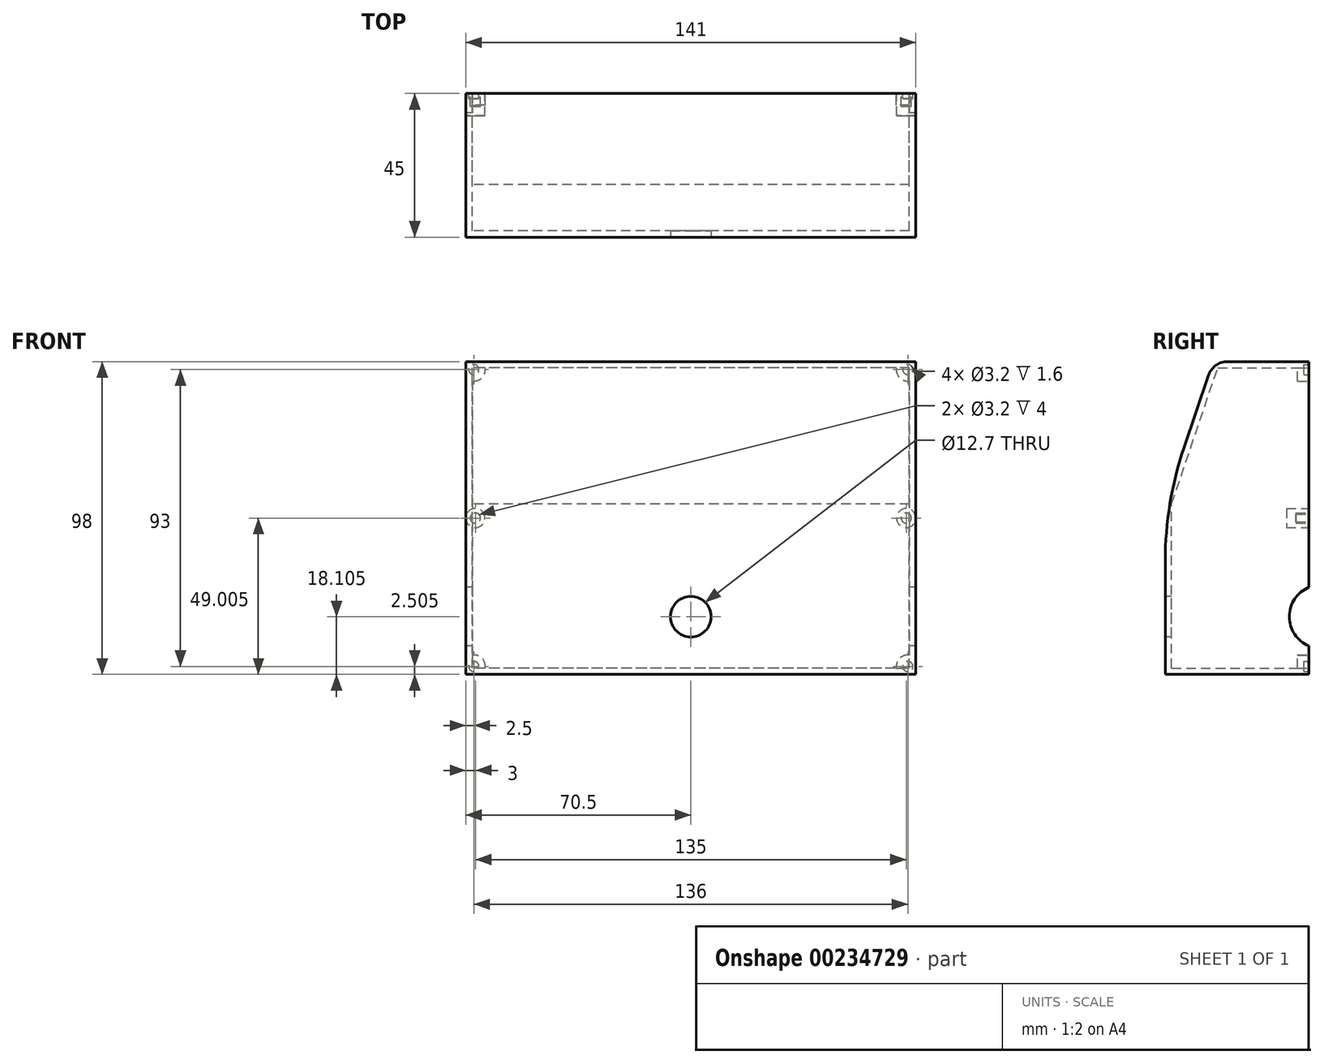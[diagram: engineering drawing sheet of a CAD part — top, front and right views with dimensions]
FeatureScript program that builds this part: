
annotation { "Feature Type Name" : "Feature", "Feature Type Description" : "" }
export const myFeature = defineFeature(function(context is Context, id is Id, definition is map)
    precondition{}
    {
        {
            var Q0;
            Q0=qCreatedBy(makeId("Right.planeOp"),FACE);
            var sketch = newSketch(context, id + "F0", { "sketchPlane" : qUnion([Q0])});
            skLineSegment(sketch, "E0.bottom", {"start": v(-27, 122.67) * mm, "end": v(33, 122.67) * mm});
            skLineSegment(sketch, "E0.top", {"start": v(-27, 24.67) * mm, "end": v(33, 24.67) * mm});
            skLineSegment(sketch, "E0.left", {"start": v(-27, 122.67) * mm, "end": v(-27, 24.67) * mm});
            skLineSegment(sketch, "E0.right", {"start": v(33, 122.67) * mm, "end": v(33, 24.67) * mm});
            skPoint(sketch, "E1", {"position": v(-12, 24.67) * mm});
            skPoint(sketch, "E2", {"position": v(-12, 78.42) * mm});
            skLineSegment(sketch, "E3", {"start": v(-12, 24.67) * mm, "end": v(-12, 78.42) * mm});
            skPoint(sketch, "E4", {"position": v(3, 122.67) * mm});
            skLineSegment(sketch, "E5", {"start": v(-12, 78.42) * mm, "end": v(3, 122.67) * mm});
            skSolve(sketch);
        }
        {
            var Q0;
            {var subQ0=sQuery(id+"F0.wireOp",EDGE,"E0.right");Q0=makeQuery(id+"F0.imprint","IMPRINT",FACE,{"disambiguationData":[TD([[makeQuery(id+"F0.imprint","IMPRINT",EDGE,{"derivedFrom":subQ0}),-1.0]])]});}
            extrude(context, id + "F1", {"entities" : qUnion([Q0]), "depth" : 141 * mm, "offsetDistance" : 25 * mm});
        }
        {
            var Q0;
            Q0=makeQuery(id+"F1.opExtrude","SWEPT_FACE",FACE,{"disambiguationData":[OSD([sQuery(id+"F0.wireOp",EDGE,"E0.right")])]});
            var sketch = newSketch(context, id + "F2", { "sketchPlane" : qUnion([Q0])});
            skCircle(sketch, "E6", {"center": v(-2.5, 27.17) * mm, "radius": 1.6 * mm});
            skCircle(sketch, "E7", {"center": v(-2.5, 27.17) * mm, "radius": 2.5 * mm});
            skCircle(sketch, "E8", {"center": v(-138.5, 120.17) * mm, "radius": 1.6 * mm});
            skCircle(sketch, "E9", {"center": v(-138.5, 120.17) * mm, "radius": 2.5 * mm});
            skCircle(sketch, "E10", {"center": v(-138.5, 27.17) * mm, "radius": 1.6 * mm});
            skCircle(sketch, "E11", {"center": v(-138.5, 27.17) * mm, "radius": 2.5 * mm});
            skPoint(sketch, "E12.centerSnap0", {"position": v(-141, 73.67) * mm});
            skPoint(sketch, "E13.centerSnap0", {"position": v(0, 73.67) * mm});
            skCircle(sketch, "E14", {"center": v(-3, 73.67) * mm, "radius": 1.6 * mm});
            skCircle(sketch, "E15", {"center": v(-3, 73.67) * mm, "radius": 3 * mm});
            skCircle(sketch, "E16", {"center": v(-138, 73.67) * mm, "radius": 1.6 * mm});
            skCircle(sketch, "E17", {"center": v(-138, 73.67) * mm, "radius": 3 * mm});
            skCircle(sketch, "E18", {"center": v(-2.5, 120.17) * mm, "radius": 1.6 * mm});
            skCircle(sketch, "E19", {"center": v(-2.5, 120.17) * mm, "radius": 2.5 * mm});
            skSolve(sketch);
        }
        {
            var Q0;
            Q0=makeQuery(id+"F2.imprint","IMPRINT",FACE,{"disambiguationData":[TD([[makeQuery(id+"F2.imprint","IMPRINT",EDGE,{"derivedFrom":sQuery(id+"F2.wireOp",EDGE,"f340615c-904d-429b-8e47-6008bda9c02a")}),1.0]])]});
            var Q1;
            Q1=makeQuery(id+"F2.imprint","IMPRINT",FACE,{"disambiguationData":[TD([[makeQuery(id+"F2.imprint","IMPRINT",EDGE,{"derivedFrom":sQuery(id+"F2.wireOp",EDGE,"E6")}),1.0]])]});
            var Q2;
            Q2=makeQuery(id+"F2.imprint","IMPRINT",FACE,{"disambiguationData":[TD([[makeQuery(id+"F2.imprint","IMPRINT",EDGE,{"derivedFrom":sQuery(id+"F2.wireOp",EDGE,"E10")}),1.0]])]});
            var Q3;
            Q3=makeQuery(id+"F2.imprint","IMPRINT",FACE,{"disambiguationData":[TD([[makeQuery(id+"F2.imprint","IMPRINT",EDGE,{"derivedFrom":sQuery(id+"F2.wireOp",EDGE,"E8")}),1.0]])]});
            var Q4;
            Q4=makeQuery(id+"F2.imprint","IMPRINT",FACE,{"disambiguationData":[TD([[makeQuery(id+"F2.imprint","IMPRINT",EDGE,{"derivedFrom":sQuery(id+"F2.wireOp",EDGE,"E18")}),1.0]])]});
            extrude(context, id + "F3", {"entities" : qUnion([Q0, Q1, Q2, Q3, Q4]), "operationType" : NewBodyOperationType.REMOVE, "oppositeDirection" : true, "depth" : 1.6 * mm, "offsetDistance" : 25 * mm});
        }
        {
            var Q0;
            Q0=makeQuery(id+"F2.imprint","IMPRINT",FACE,{"disambiguationData":[TD([[makeQuery(id+"F2.imprint","IMPRINT",EDGE,{"derivedFrom":sQuery(id+"F2.wireOp",EDGE,"E16")}),-1.0]])]});
            var Q1;
            Q1=makeQuery(id+"F2.imprint","IMPRINT",FACE,{"disambiguationData":[TD([[makeQuery(id+"F2.imprint","IMPRINT",EDGE,{"derivedFrom":sQuery(id+"F2.wireOp",EDGE,"E16")}),1.0]])]});
            var Q2;
            Q2=makeQuery(id+"F2.imprint","IMPRINT",FACE,{"disambiguationData":[TD([[makeQuery(id+"F2.imprint","IMPRINT",EDGE,{"derivedFrom":sQuery(id+"F2.wireOp",EDGE,"E14")}),1.0]])]});
            var Q3;
            Q3=makeQuery(id+"F2.imprint","IMPRINT",FACE,{"disambiguationData":[TD([[makeQuery(id+"F2.imprint","IMPRINT",EDGE,{"derivedFrom":sQuery(id+"F2.wireOp",EDGE,"E14")}),-1.0]])]});
            extrude(context, id + "F4", {"entities" : qUnion([Q0, Q1, Q2, Q3]), "depth" : -7 * mm, "offsetDistance" : 25 * mm});
        }
        {
            var Q0;
            Q0=makeQuery(id+"F1.opExtrude","SWEPT_FACE",FACE,{"disambiguationData":[OSD([sQuery(id+"F0.wireOp",EDGE,"E0.right")])]});
            shell(context, id + "F5", {"entities" : qUnion([Q0]), "thickness" : 2 * mm});
        }
        {
            var Q0;
            Q0=makeQuery(id+"F2.imprint","IMPRINT",FACE,{"disambiguationData":[TD([[makeQuery(id+"F2.imprint","IMPRINT",EDGE,{"derivedFrom":sQuery(id+"F2.wireOp",EDGE,"E16")}),1.0]])]});
            var Q1;
            Q1=makeQuery(id+"F2.imprint","IMPRINT",FACE,{"disambiguationData":[TD([[makeQuery(id+"F2.imprint","IMPRINT",EDGE,{"derivedFrom":sQuery(id+"F2.wireOp",EDGE,"E14")}),1.0]])]});
            extrude(context, id + "F6", {"entities" : qUnion([Q0, Q1]), "operationType" : NewBodyOperationType.REMOVE, "depth" : -4 * mm, "offsetDistance" : 25 * mm});
        }
        {
            var Q0;
            Q0=makeQuery(id+"F1.opExtrude","CAP_FACE",FACE,{"disambiguationData":[OSD([sQuery(id+"F0.wireOp",EDGE,"E0.bottom"),sQuery(id+"F0.wireOp",EDGE,"E0.top"),sQuery(id+"F0.wireOp",EDGE,"E0.left"),sQuery(id+"F0.wireOp",EDGE,"E0.right"),sQuery(id+"F0.wireOp",EDGE,"4a58c281-0875-4a74-9afb-d6dd05803dfe"),sQuery(id+"F0.wireOp",EDGE,"33c9b275-3f99-4670-a69c-7fdbbfd8911e")])],"isStart":true});
            var sketch = newSketch(context, id + "F7", { "sketchPlane" : qUnion([Q0])});
            skCircle(sketch, "E20", {"center": v(-36.9, 42.77) * mm, "radius": 10 * mm});
            skSolve(sketch);
        }
        {
            var Q0;
            {var subQ0=sQuery(id+"F7.wireOp",EDGE,"E20");var subQ1=makeQuery(id+"F1.opExtrude","CAP_EDGE",EDGE,{"disambiguationData":[OSD([sQuery(id+"F0.wireOp",EDGE,"E0.right")])],"isStart":true});var subQ2=makeQuery(id+"F7.imprint","INTERSECT",VERTEX,{"disambiguationData":[OD(0.0)],"derivedFrom":[subQ1,subQ0]});Q0=makeQuery(id+"F7.imprint","IMPRINT",FACE,{"disambiguationData":[TD([[makeQuery(id+"F7.imprint","IMPRINT",EDGE,{"disambiguationData":[TD([[subQ2,1.0]])],"derivedFrom":subQ0}),1.0]])]});}
            var Q1;
            {var subQ0=sQuery(id+"F7.wireOp",EDGE,"E20");var subQ1=makeQuery(id+"F1.opExtrude","CAP_EDGE",EDGE,{"disambiguationData":[OSD([sQuery(id+"F0.wireOp",EDGE,"E0.right")])],"isStart":true});var subQ2=makeQuery(id+"F7.imprint","INTERSECT",VERTEX,{"disambiguationData":[OD(0.0)],"derivedFrom":[subQ1,subQ0]});Q1=makeQuery(id+"F7.imprint","IMPRINT",FACE,{"disambiguationData":[TD([[makeQuery(id+"F7.imprint","IMPRINT",EDGE,{"disambiguationData":[TD([[subQ2,-1.0]])],"derivedFrom":subQ0}),1.0]])]});}
            extrude(context, id + "F8", {"entities" : qUnion([Q0, Q1]), "operationType" : NewBodyOperationType.REMOVE, "oppositeDirection" : true, "depth" : 150 * mm, "offsetDistance" : 25 * mm});
        }
        {
            var Q0;
            Q0=makeQuery(id+"F1.opExtrude","SWEPT_FACE",FACE,{"disambiguationData":[OSD([sQuery(id+"F0.wireOp",EDGE,"E3")])]});
            var sketch = newSketch(context, id + "F9", { "sketchPlane" : qUnion([Q0])});
            skCircle(sketch, "E21", {"center": v(70.5, 42.77) * mm, "radius": 6.35 * mm});
            skSolve(sketch);
        }
        {
            var Q0;
            Q0=makeQuery(id+"F9.imprint","IMPRINT",FACE,{"disambiguationData":[TD([[makeQuery(id+"F9.imprint","IMPRINT",EDGE,{"derivedFrom":sQuery(id+"F9.wireOp",EDGE,"E21")}),1.0]])]});
            extrude(context, id + "F10", {"entities" : qUnion([Q0]), "operationType" : NewBodyOperationType.REMOVE, "oppositeDirection" : true, "depth" : 50 * mm, "offsetDistance" : 25 * mm});
        }
        {
            var Q0;
            Q0=makeQuery(id+"F1.opExtrude","SWEPT_EDGE",EDGE,{"disambiguationData":[OSD([sQuery(id+"F0.wireOp",EDGE,"E0.bottom"),sQuery(id+"F0.wireOp",EDGE,"E5")])]});
            fillet(context, id + "F11", {"entities" : qUnion([Q0]), "tangentPropagation" : true, "radius" : 6.34 * mm, "defaultsChanged" : true, "vertexSettings" : [], "allowEdgeOverflow" : false});
        }
        {
            var Q0;
            Q0=makeQuery(id+"F1.opExtrude","SWEPT_EDGE",EDGE,{"disambiguationData":[OSD([sQuery(id+"F0.wireOp",EDGE,"E3"),sQuery(id+"F0.wireOp",EDGE,"E5")])]});
            fillet(context, id + "F12", {"entities" : qUnion([Q0]), "tangentPropagation" : true, "radius" : 110.7 * mm, "defaultsChanged" : false, "vertexSettings" : [], "allowEdgeOverflow" : false});
        }
    });
